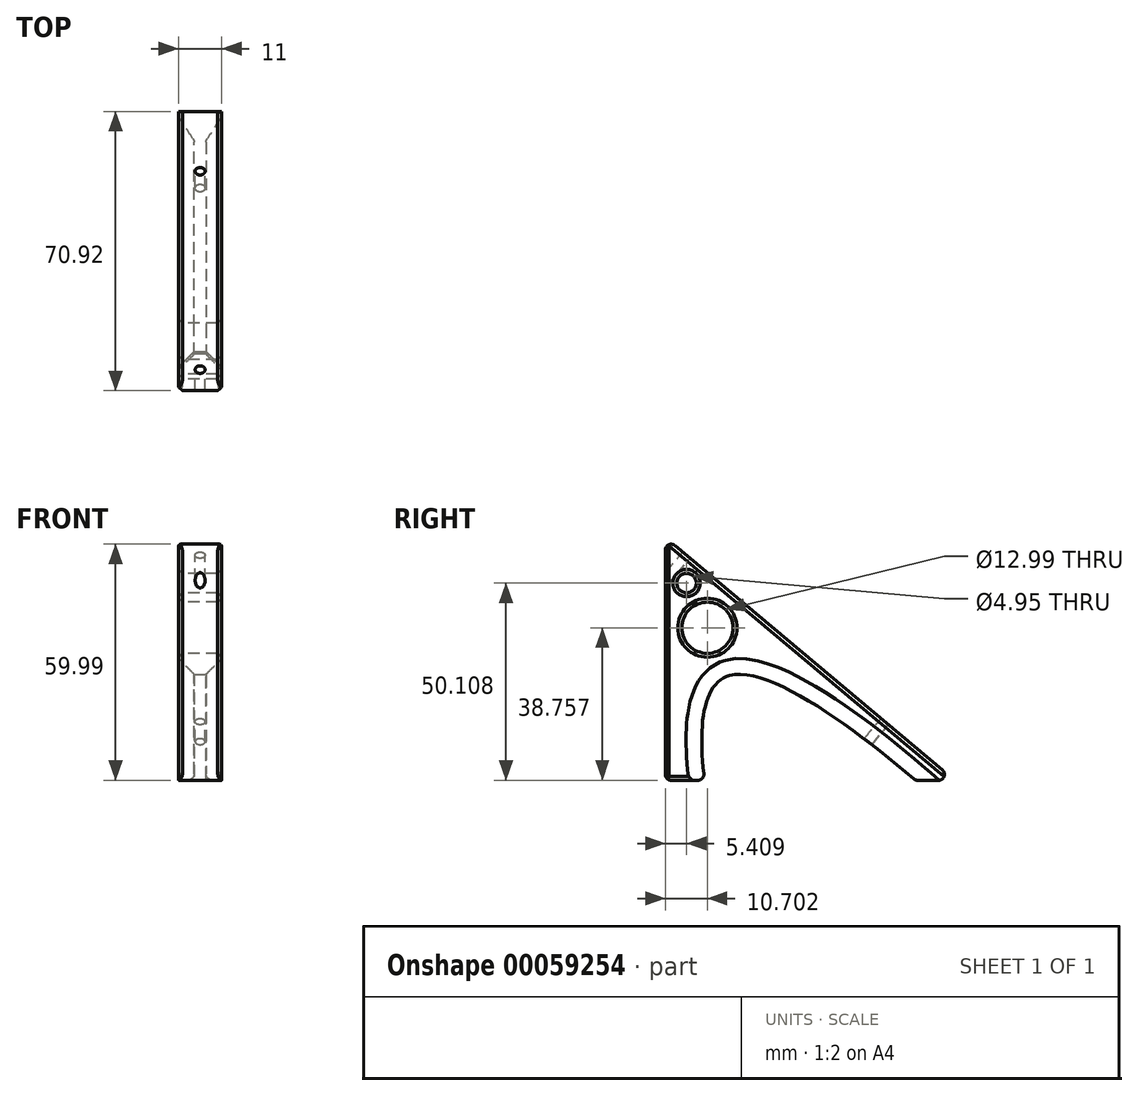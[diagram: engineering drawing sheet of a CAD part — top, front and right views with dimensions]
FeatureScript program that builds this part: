
annotation { "Feature Type Name" : "Feature", "Feature Type Description" : "" }
export const myFeature = defineFeature(function(context is Context, id is Id, definition is map)
    precondition{}
    {
        {
            var Q0;
            Q0=qCreatedBy(makeId("Right.planeOp"),FACE);
            var sketch = newSketch(context, id + "F0", { "sketchPlane" : qUnion([Q0])});
            skLineSegment(sketch, "E0", {"start": v(0, 0) * mm, "end": v(0, 61.7) * mm});
            skLineSegment(sketch, "E1", {"start": v(0, 61.7) * mm, "end": v(73.54, 0) * mm});
            skLineSegment(sketch, "E2", {"start": v(73.54, 0) * mm, "end": v(63.54, 0) * mm});
            skFitSpline(sketch, "E3", {"points": [v(63.54, 0) * mm, v(16.35, 26.64) * mm, v(10, 0) * mm], "startDerivative": vector(-80.73, 69.49) * mm, "endDerivative": vector(12.59, -97.14) * mm});
            skLineSegment(sketch, "E4", {"start": v(10, 0) * mm, "end": v(0, 0) * mm});
            skCircle(sketch, "E5", {"center": v(10.7, 38.76) * mm, "radius": 6.5 * mm});
            skCircle(sketch, "E6", {"center": v(5.4, 50.1) * mm, "radius": 2.47 * mm});
            skLineSegment(sketch, "E7", {"start": v(0, 61.7) * mm, "end": v(25.01, 8.06) * mm});
            skSolve(sketch);
        }
        {
            var Q0;
            Q0 = qSketchRegion(id + "F0", true);
            extrude(context, id + "F1", {"entities" : qUnion([Q0]), "depth" : 11 * mm});
        }
        {
            var Q0;
            Q0=makeQuery(id+"F1.opExtrude","CAP_EDGE",EDGE,{"disambiguationData":[OSD([sQuery(id+"F0.wireOp",EDGE,"E3")])],"isStart":false});
            var Q1;
            Q1=makeQuery(id+"F1.opExtrude","CAP_EDGE",EDGE,{"disambiguationData":[OSD([sQuery(id+"F0.wireOp",EDGE,"E3")])],"isStart":true});
            chamfer(context, id + "F2", {"entities" : qUnion([Q0, Q1]), "width" : 4 * mm, "tangentPropagation" : true});
        }
        {
            var Q0;
            Q0=makeQuery(id+"F1.opExtrude","CAP_EDGE",EDGE,{"disambiguationData":[OSD([sQuery(id+"F0.wireOp",EDGE,"E6")])],"isStart":true});
            var Q1;
            Q1=makeQuery(id+"F1.opExtrude","CAP_EDGE",EDGE,{"disambiguationData":[OSD([sQuery(id+"F0.wireOp",EDGE,"E5")])],"isStart":true});
            var Q2;
            Q2=makeQuery(id+"F1.opExtrude","CAP_EDGE",EDGE,{"disambiguationData":[OSD([sQuery(id+"F0.wireOp",EDGE,"E5")])],"isStart":false});
            var Q3;
            Q3=makeQuery(id+"F1.opExtrude","CAP_EDGE",EDGE,{"disambiguationData":[OSD([sQuery(id+"F0.wireOp",EDGE,"E6")])],"isStart":false});
            chamfer(context, id + "F3", {"entities" : qUnion([Q0, Q1, Q2, Q3]), "width" : 1 * mm, "tangentPropagation" : true});
        }
        {
            var Q0;
            Q0=makeQuery(id+"F1.opExtrude","SWEPT_FACE",FACE,{"disambiguationData":[OSD([sQuery(id+"F0.wireOp",EDGE,"E1")])]});
            var sketch = newSketch(context, id + "F4", { "sketchPlane" : qUnion([Q0])});
            skCircle(sketch, "E8", {"center": v(5.5, -32.66) * mm, "radius": 1.25 * mm});
            skCircle(sketch, "E9", {"center": v(5.5, 33.14) * mm, "radius": 1.25 * mm});
            skLineSegment(sketch, "E10", {"start": v(5.5, -39.66) * mm, "end": v(5.5, 30.13) * mm, "construction": true});
            skPoint(sketch, "E10.endSnap0", {"position": v(5.5, 56.34) * mm});
            skSolve(sketch);
        }
        {
            var Q0;
            Q0 = qSketchRegion(id + "F4", true);
            extrude(context, id + "F5", {"entities" : qUnion([Q0]), "operationType" : NewBodyOperationType.REMOVE, "endBound" : BoundingType.THROUGH_ALL, "oppositeDirection" : true, "depth" : 5.5 * mm});
        }
        {
            var Q0;
            Q0=makeQuery(id+"F1.opExtrude","CAP_EDGE",EDGE,{"disambiguationData":[OSD([sQuery(id+"F0.wireOp",EDGE,"E0")])],"isStart":false});
            var Q1;
            Q1=makeQuery(id+"F1.opExtrude","CAP_EDGE",EDGE,{"disambiguationData":[OSD([sQuery(id+"F0.wireOp",EDGE,"E0")])],"isStart":true});
            var Q2;
            Q2=makeQuery(id+"F1.opExtrude","CAP_EDGE",EDGE,{"disambiguationData":[OSD([sQuery(id+"F0.wireOp",EDGE,"E1")])],"isStart":true});
            var Q3;
            Q3=makeQuery(id+"F1.opExtrude","CAP_EDGE",EDGE,{"disambiguationData":[OSD([sQuery(id+"F0.wireOp",EDGE,"E4")])],"isStart":true});
            var Q4;
            Q4=makeQuery(id+"F1.opExtrude","CAP_EDGE",EDGE,{"disambiguationData":[OSD([sQuery(id+"F0.wireOp",EDGE,"E1")])],"isStart":false});
            var Q5;
            Q5=makeQuery(id+"F1.opExtrude","CAP_EDGE",EDGE,{"disambiguationData":[OSD([sQuery(id+"F0.wireOp",EDGE,"E4")])],"isStart":false});
            chamfer(context, id + "F6", {"entities" : qUnion([Q0, Q1, Q2, Q3, Q4, Q5]), "width" : 1 * mm, "tangentPropagation" : true});
        }
        {
            var Q0;
            Q0=makeQuery(id+"F1.opExtrude","SWEPT_EDGE",EDGE,{"disambiguationData":[OSD([sQuery(id+"F0.wireOp",EDGE,"E1"),sQuery(id+"F0.wireOp",EDGE,"E2")])]});
            var Q1;
            Q1=makeQuery(id+"F1.opExtrude","SWEPT_EDGE",EDGE,{"disambiguationData":[OSD([sQuery(id+"F0.wireOp",EDGE,"E0"),sQuery(id+"F0.wireOp",EDGE,"E1"),sQuery(id+"F0.wireOp",EDGE,"E7")])]});
            var Q2;
            Q2=makeQuery(id+"F1.opExtrude","SWEPT_EDGE",EDGE,{"disambiguationData":[OSD([sQuery(id+"F0.wireOp",EDGE,"E2"),sQuery(id+"F0.wireOp",EDGE,"E3")])]});
            var Q3;
            Q3=makeQuery(id+"F1.opExtrude","SWEPT_EDGE",EDGE,{"disambiguationData":[OSD([sQuery(id+"F0.wireOp",EDGE,"E3"),sQuery(id+"F0.wireOp",EDGE,"E4")])]});
            var Q4;
            Q4=makeQuery(id+"F1.opExtrude","SWEPT_EDGE",EDGE,{"disambiguationData":[OSD([sQuery(id+"F0.wireOp",EDGE,"E0"),sQuery(id+"F0.wireOp",EDGE,"E4")])]});
            fillet(context, id + "F7", {"entities" : qUnion([Q0, Q1, Q2, Q3, Q4]), "radius" : 1.5 * mm, "tangentPropagation" : true, "allowEdgeOverflow" : false});
        }
    });
